SOLIDWORKS PART (.sldprt)
format: sldprt  version: not decoded by parser v0  size: 87,552 bytes
history: native  units: mm
features: plane x3, sketch x2, extrude x2, material x1, chamfer x1 (+9 scaffold rows collapsed)
feature tree (18):
  scaffold x9  (default folders/planes/origin — collapsed)
  material  "Material <not specified>"
  plane  "Face"
  plane  "Dessus"
  plane  "Droite"
  sketch  "Esquisse1"  dims[D3=~5.430641mm D1=2.51mm D2=2.51mm]
  extrude  "Extrusion1"  Depth=2.15mm
  sketch  "Esquisse2"  dims[D1=0.8mm]
  extrude  "Extrusion2"  Depth=2mm
  chamfer  "Chanfrein1"  Distance=0.25mm Angle=45deg
decode coverage: 5 of 5 modeling features carry decoded parameters
note: ~ marks probable driven/reference dimensions
note: suppression state not decoded; provenance and decode notes live in map.json
